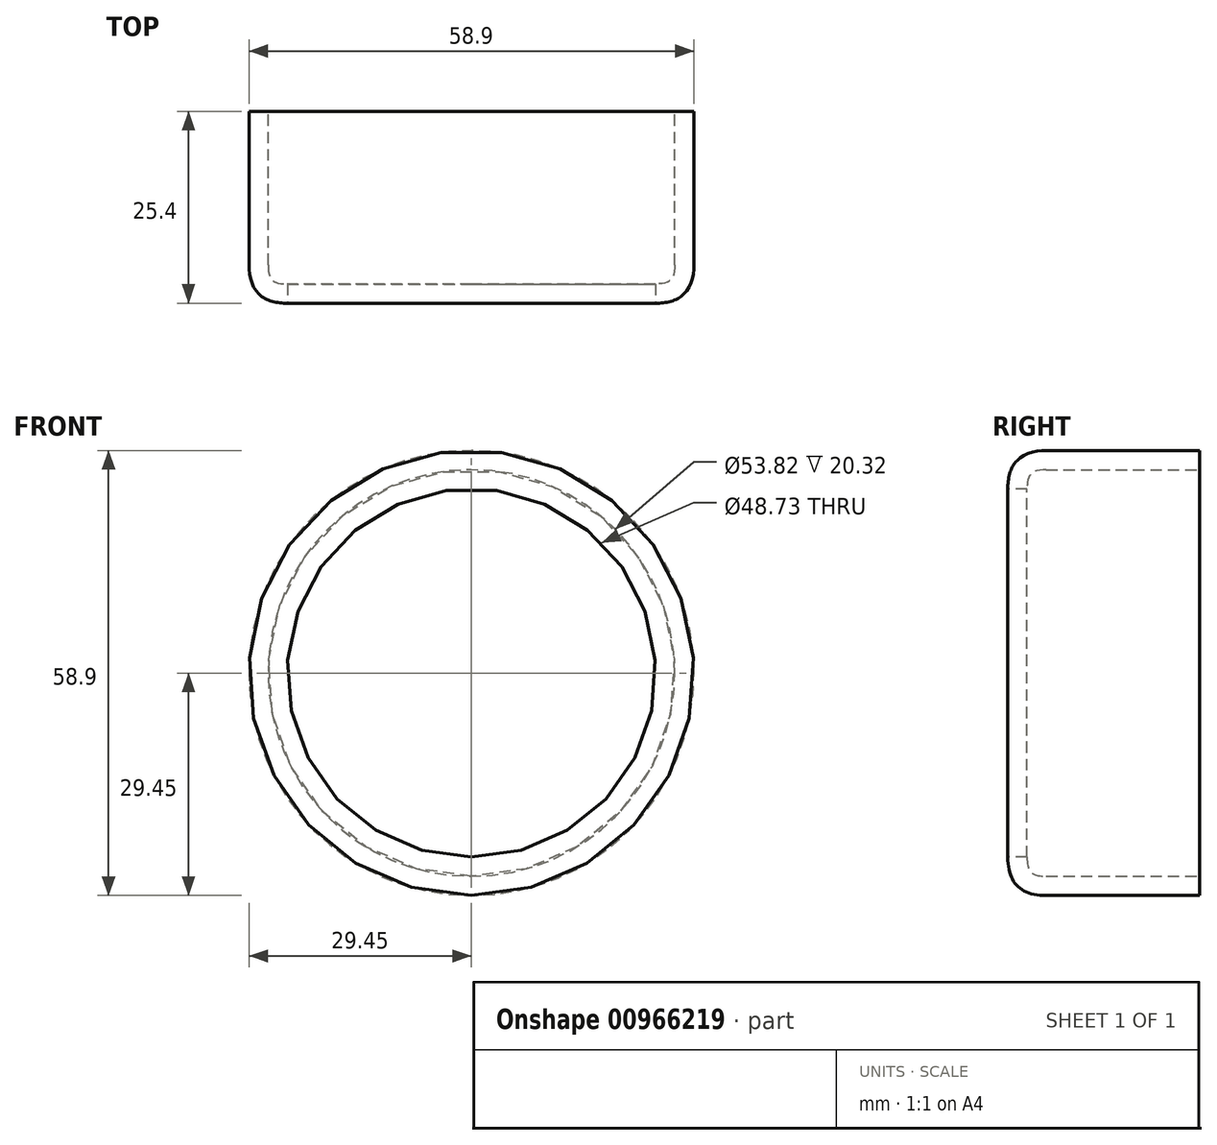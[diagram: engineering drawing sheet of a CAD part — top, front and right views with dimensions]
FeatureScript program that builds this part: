
annotation { "Feature Type Name" : "Feature", "Feature Type Description" : "" }
export const myFeature = defineFeature(function(context is Context, id is Id, definition is map)
    precondition{}
    {
        {
            var Q0;
            Q0=qCreatedBy(makeId("Front.planeOp"),FACE);
            var sketch = newSketch(context, id + "F0", { "sketchPlane" : qUnion([Q0])});
            skCircle(sketch, "E0", {"center": v(0, 0) * mm, "radius": 29.45 * mm});
            skSolve(sketch);
        }
        {
            var Q0;
            Q0=makeQuery(id+"F0.imprint","IMPRINT",FACE,{"disambiguationData":[TD([[makeQuery(id+"F0.imprint","IMPRINT",EDGE,{"derivedFrom":sQuery(id+"F0.wireOp",EDGE,"E0")}),1.0]])]});
            extrude(context, id + "F1", {"entities" : qUnion([Q0]), "depth" : 25.4 * mm, "offsetDistance" : 25.4 * mm});
        }
        {
            var Q0;
            Q0=makeQuery(id+"F1.opExtrude","CAP_EDGE",EDGE,{"disambiguationData":[OSD([sQuery(id+"F0.wireOp",EDGE,"E0")])],"isStart":false});
            fillet(context, id + "F2", {"entities" : qUnion([Q0]), "radius" : 5.08 * mm, "tangentPropagation" : true, "rho" : 0.5, "crossSection" : FilletCrossSection.CONIC, "allowEdgeOverflow" : false});
        }
        {
            var Q0;
            Q0=makeQuery(id+"F1.opExtrude","CAP_FACE",FACE,{"disambiguationData":[OSD([sQuery(id+"F0.wireOp",EDGE,"E0")])],"isStart":true});
            shell(context, id + "F3", {"entities" : qUnion([Q0]), "thickness" : 2.54 * mm});
        }
        {
            var Q0;
            Q0=makeQuery(id+"F1.opExtrude","CAP_FACE",FACE,{"disambiguationData":[OSD([sQuery(id+"F0.wireOp",EDGE,"E0")])],"isStart":false});
            extrude(context, id + "F4", {"entities" : qUnion([Q0]), "operationType" : NewBodyOperationType.REMOVE, "oppositeDirection" : true, "depth" : 15.75 * mm, "offsetDistance" : 25.4 * mm});
        }
    });
